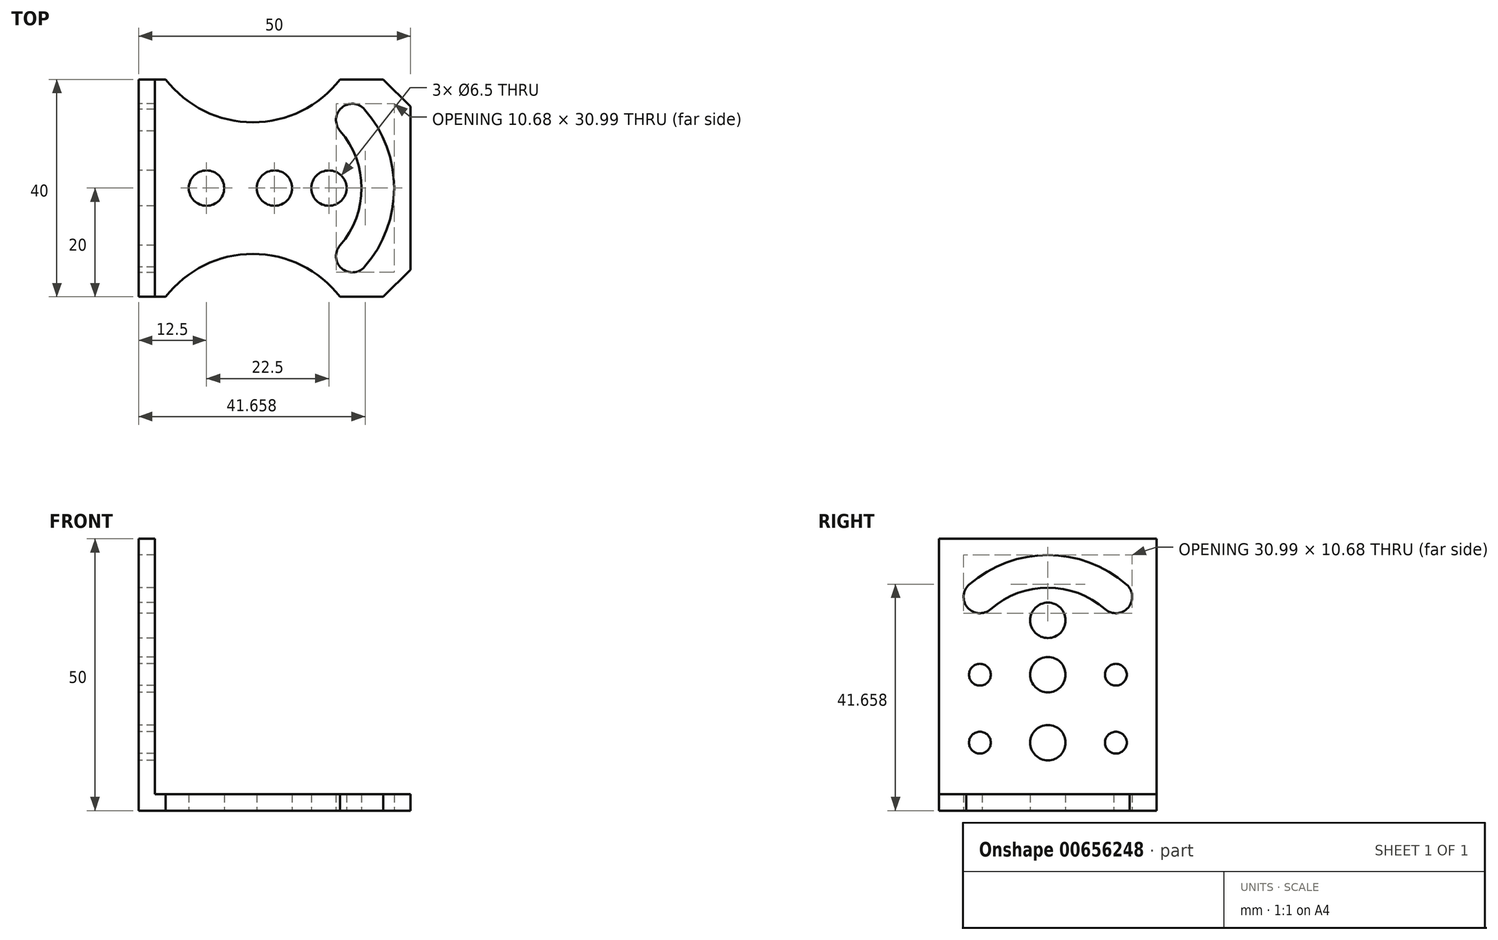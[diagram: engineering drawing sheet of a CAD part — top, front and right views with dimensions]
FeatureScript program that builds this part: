
annotation { "Feature Type Name" : "Feature", "Feature Type Description" : "" }
export const myFeature = defineFeature(function(context is Context, id is Id, definition is map)
    precondition{}
    {
        {
            var Q0;
            Q0=qCreatedBy(makeId("Front.planeOp"),FACE);
            var sketch = newSketch(context, id + "F0", { "sketchPlane" : qUnion([Q0])});
            skLineSegment(sketch, "E0", {"start": v(0, 0) * mm, "end": v(50, 0) * mm});
            skLineSegment(sketch, "E1", {"start": v(50, 0) * mm, "end": v(50, 5) * mm});
            skLineSegment(sketch, "E2", {"start": v(50, 5) * mm, "end": v(5, 5) * mm});
            skLineSegment(sketch, "E3", {"start": v(5, 5) * mm, "end": v(5, 50) * mm});
            skLineSegment(sketch, "E4", {"start": v(5, 50) * mm, "end": v(0, 50) * mm});
            skLineSegment(sketch, "E5", {"start": v(0, 50) * mm, "end": v(0, 0) * mm});
            skSolve(sketch);
        }
        {
            var Q0;
            Q0=qSketchRegion(id+"F0",true);
            extrude(context, id + "F1", {"entities" : qUnion([Q0]), "depth" : 40 * mm, "offsetDistance" : 25 * mm});
        }
        {
            var Q0;
            Q0=makeQuery(id+"F1.opExtrude","SWEPT_FACE",FACE,{"disambiguationData":[OSD([sQuery(id+"F0.wireOp",EDGE,"E0")])]});
            var sketch = newSketch(context, id + "F2", { "sketchPlane" : qUnion([Q0])});
            skCircle(sketch, "E6", {"center": v(25, 20) * mm, "radius": 3.25 * mm});
            skPoint(sketch, "E6.centerSnap0", {"position": v(0, 20) * mm});
            skArc(sketch, "E7", {"start": v(37.05, 9.47) * mm, "mid": v(37.34, 5.24) * mm, "end": v(41.57, 5.53) * mm});
            skArc(sketch, "E8", {"start": v(41.57, 34.47) * mm, "mid": v(37.34, 34.76) * mm, "end": v(37.05, 30.53) * mm});
            skArc(sketch, "E9", {"start": v(37.05, 9.47) * mm, "mid": v(41, 20) * mm, "end": v(37.05, 30.53) * mm});
            skArc(sketch, "E10", {"start": v(41.57, 5.53) * mm, "mid": v(47, 20) * mm, "end": v(41.57, 34.47) * mm});
            skCircle(sketch, "E11", {"center": v(12.5, 20) * mm, "radius": 3.25 * mm});
            skCircle(sketch, "E12", {"center": v(35, 20) * mm, "radius": 3.25 * mm});
            skPoint(sketch, "E12.centerSnap0", {"position": v(41, 20) * mm});
            skArc(sketch, "E13", {"start": v(37.05, 0) * mm, "mid": v(21.02, 7.9) * mm, "end": v(5, 0) * mm});
            skArc(sketch, "E14", {"start": v(5, 40) * mm, "mid": v(21.02, 32.1) * mm, "end": v(37.05, 40) * mm});
            skLineSegment(sketch, "E15", {"start": v(37.05, 0) * mm, "end": v(26.55, -9.52) * mm});
            skLineSegment(sketch, "E16", {"start": v(26.55, -9.52) * mm, "end": v(5, 0) * mm});
            skLineSegment(sketch, "E17", {"start": v(5, 40) * mm, "end": v(21.02, 52.32) * mm});
            skLineSegment(sketch, "E18", {"start": v(37.05, 40) * mm, "end": v(21.02, 52.32) * mm});
            skSolve(sketch);
        }
        {
            var Q0;
            Q0=qSketchRegion(id+"F2",true);
            extrude(context, id + "F3", {"entities" : qUnion([Q0]), "operationType" : NewBodyOperationType.REMOVE, "oppositeDirection" : true, "depth" : 25 * mm, "offsetDistance" : 25 * mm});
        }
        {
            var Q0;
            Q0=makeQuery(id+"F1.opExtrude","SWEPT_FACE",FACE,{"disambiguationData":[OSD([sQuery(id+"F0.wireOp",EDGE,"E5")])]});
            var sketch = newSketch(context, id + "F4", { "sketchPlane" : qUnion([Q0])});
            skCircle(sketch, "E19", {"center": v(20, 12.5) * mm, "radius": 3.25 * mm});
            skPoint(sketch, "E19.centerSnap0", {"position": v(20, 0) * mm});
            skCircle(sketch, "E20", {"center": v(20, 25) * mm, "radius": 3.25 * mm});
            skCircle(sketch, "E21", {"center": v(20, 35) * mm, "radius": 3.25 * mm});
            skArc(sketch, "E22", {"start": v(30.53, 37.05) * mm, "mid": v(20, 41) * mm, "end": v(9.47, 37.05) * mm});
            skArc(sketch, "E23", {"start": v(5.53, 41.57) * mm, "mid": v(5.24, 37.34) * mm, "end": v(9.47, 37.05) * mm});
            skArc(sketch, "E24", {"start": v(30.53, 37.05) * mm, "mid": v(34.76, 37.34) * mm, "end": v(34.47, 41.57) * mm});
            skArc(sketch, "E25", {"start": v(34.47, 41.57) * mm, "mid": v(20, 47) * mm, "end": v(5.53, 41.57) * mm});
            skCircle(sketch, "E26", {"center": v(32.5, 12.5) * mm, "radius": 2 * mm});
            skCircle(sketch, "E27", {"center": v(32.5, 25) * mm, "radius": 2 * mm});
            skCircle(sketch, "E28", {"center": v(7.5, 25) * mm, "radius": 2 * mm});
            skCircle(sketch, "E29", {"center": v(7.5, 12.5) * mm, "radius": 2 * mm});
            skSolve(sketch);
        }
        {
            var Q0;
            Q0=qSketchRegion(id+"F4",true);
            extrude(context, id + "F5", {"entities" : qUnion([Q0]), "operationType" : NewBodyOperationType.REMOVE, "oppositeDirection" : true, "depth" : 25 * mm, "offsetDistance" : 25 * mm});
        }
        {
            var Q0;
            Q0=makeQuery(id+"F1.opExtrude","CAP_EDGE",EDGE,{"disambiguationData":[OSD([sQuery(id+"F0.wireOp",EDGE,"E1")])],"isStart":false});
            chamfer(context, id + "F6", {"entities" : qUnion([Q0]), "width" : 5 * mm, "tangentPropagation" : true});
        }
        {
            var Q0;
            Q0=makeQuery(id+"F1.opExtrude","CAP_EDGE",EDGE,{"disambiguationData":[OSD([sQuery(id+"F0.wireOp",EDGE,"E1")])],"isStart":true});
            chamfer(context, id + "F7", {"entities" : qUnion([Q0]), "width" : 5 * mm, "tangentPropagation" : true});
        }
        {
            var Q0;
            Q0 = qSketchRegion(id + "F2", true);
            extrude(context, id + "F8", {"entities" : qUnion([Q0]), "operationType" : NewBodyOperationType.REMOVE, "depth" : 25 * mm, "offsetDistance" : 25 * mm});
        }
        {
            var Q0;
            {var subQ0=sQuery(id+"F0.wireOp",EDGE,"E4");var subQ1=sQuery(id+"F0.wireOp",EDGE,"E2");var subQ2=sQuery(id+"F0.wireOp",EDGE,"E3");var subQ3=sQuery(id+"F0.wireOp",EDGE,"E0");var subQ4=sQuery(id+"F0.wireOp",EDGE,"E5");Q0=makeQuery(id+"F3.boolean.opBoolean","SPLIT",FACE,{"disambiguationData":[TD([makeQuery(id+"F1.opExtrude","SWEPT_FACE",FACE,{"disambiguationData":[OSD([subQ2])]})])],"derivedFrom":makeQuery(id+"F1.opExtrude","CAP_FACE",FACE,{"disambiguationData":[OSD([subQ3,sQuery(id+"F0.wireOp",EDGE,"E1"),subQ1,subQ2,subQ0,subQ4])],"isStart":false})});}
            var sketch = newSketch(context, id + "F9", { "sketchPlane" : qUnion([Q0])});
            skLineSegment(sketch, "E30.bottom", {"start": v(3, 3) * mm, "end": v(53.79, 3) * mm});
            skLineSegment(sketch, "E30.top", {"start": v(3, 60.6) * mm, "end": v(53.79, 60.6) * mm});
            skLineSegment(sketch, "E30.left", {"start": v(3, 3) * mm, "end": v(3, 60.6) * mm});
            skLineSegment(sketch, "E30.right", {"start": v(53.79, 3) * mm, "end": v(53.79, 60.6) * mm});
            skSolve(sketch);
        }
        {
            var Q0;
            Q0 = qSketchRegion(id + "F9", true);
            extrude(context, id + "F10", {"entities" : qUnion([Q0]), "operationType" : NewBodyOperationType.REMOVE, "oppositeDirection" : true, "depth" : 51.1 * mm, "offsetDistance" : 25 * mm});
        }
    });
